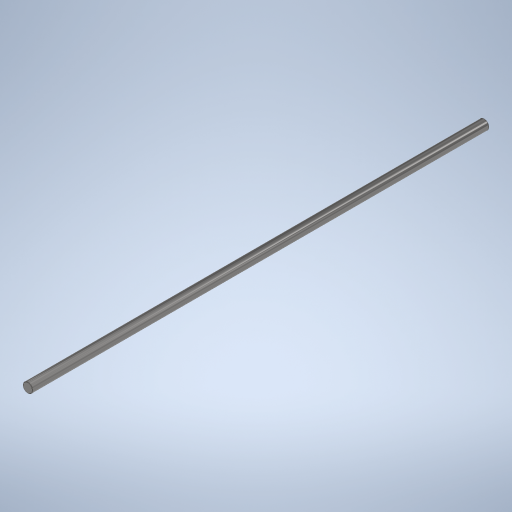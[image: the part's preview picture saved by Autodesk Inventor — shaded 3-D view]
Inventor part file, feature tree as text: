
AUTODESK INVENTOR PART (.ipt)
format: ipt  version: 2024 (Build 280153000, 153)  size: 261,120 bytes
history: native  units: mm
features: other x1, extrude x1, chamfer x1, sketch x1
ambient origin geometry x8: Origin, YZ Plane, XZ Plane, XY Plane, X Axis, Y Axis, Z Axis, Center Point
bodies: Body1 (feature_tree)
feature tree (4):
  other  "Bryła1"
  extrude  "Wyciągnięcie proste1"  Depth=12.0mm
  chamfer  "Faza1"  Distance=564.0mm
  sketch  "Szkic1"
